# Revit family: Toilet_Seat-Round-American_Standard-Champion-5320B65CT_Series
name_source: partatom
category: Specialty Equipment
revit_build: Autodesk Revit 2018 (Build: 20170223_1515(x64)
units: mm (PartAtom-declared; Revit-internal decimal feet)

## family parameters
Always vertical = No
Cut with Voids When Loaded = No
OmniClass Number = 23.45.05.21.14.11
OmniClass Title = Water Closet Seats
Part Type = Normal
Room Calculation Point = No
Round Connector Dimension = Use Diameter
Shared = Yes
Work Plane-Based = Yes

## types (3) — shared parameters
Assembly Code = D2010110
Default Elevation = 0"
Description = Champion® Slow-Close & Easy Lift-Off Round Front Toilet Seat
Installation Type = Surface Mounted
Length = 16 13/16"
Manufacturer = American Standard
Product Documentation Link = https://americanstandard.box.com
Product Page URL = https://www.americanstandard-us.com
URL = http://www.americanstandard-us.com
Width = 14 5/16"

## per-type parameters (varying)
| type | Finish | Material |
| 5320B65CT.020 | Plastic-American Standard-020-White | Plastic-American Standard-020-White |
| 5320B65CT.222 | Plastic-American Standard-222-Linen | Plastic-American Standard-222-Linen |
| 5320B65CT.021 | Plastic-American Standard-021-Bone | Plastic-American Standard-021-Bone |

note: column(s) folded — value = type name in every type: Model

## geometry (parser evidence)
native form markers: Sweep x2
no freeform markers — native parametric forms only
